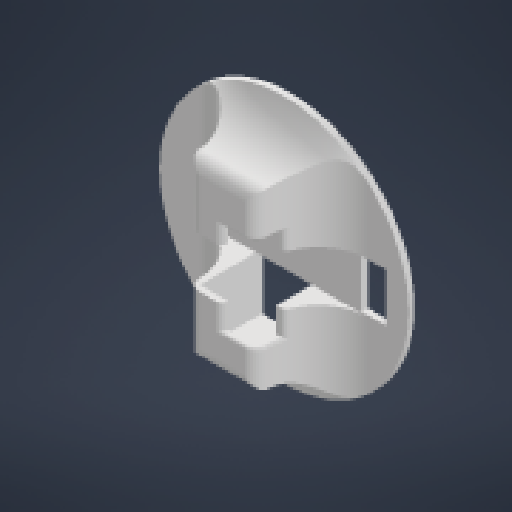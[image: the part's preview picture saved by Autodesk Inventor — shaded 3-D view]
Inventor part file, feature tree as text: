
AUTODESK INVENTOR PART (.ipt)
format: ipt  version: 2023 (Build 270158000, 158)  size: 404,480 bytes
history: native  units: mm
features: sketch x7, extrude x6, fillet x5
ambient origin geometry x8: Origin, YZ Plane, XZ Plane, XY Plane, X Axis, Y Axis, Z Axis, Center Point
bodies: Solid1 (feature_tree)
feature tree (18):
  extrude  "Extrusion1"  Depth=5.0mm TaperAngle=0.0deg
  extrude  "Extrusion2"  Depth=45.0mm
  extrude  "Extrusion3"  Depth=45.0mm
  fillet  "Fillet1"  Radius=40.0mm
  fillet  "Fillet2"  Radius=5.0mm
  extrude  "Extrusion4"  Depth=50.0mm TaperAngle=0.0deg
  extrude  "Extrusion5"  TaperAngle=90.0deg  [1 undecoded]
  fillet  "Fillet3"  Radius=22.5mm
  fillet  "Fillet4"  Radius=45.0mm
  fillet  "Fillet5"  Radius=45.0mm
  extrude  "Extrusion6"  Depth=50.0mm TaperAngle=0.0deg
  sketch  "Sketch7"  dims[d24=40.0mm d25=10.0mm d26=75.0mm d27=9.0mm d28=0.0mm d29=9.0mm d30=0.0mm d31=5.0mm d32=5.0mm d33=2.0mm d34=9.0mm d35=0.0mm d36=180.0deg]
  sketch  "Sketch1"  dims[d0=200.0mm d1=5.0mm d2=0.0mm]
  sketch  "Sketch2"  dims[d5=22.5mm d6=45.0mm]
  sketch  "Sketch3"  dims[d7=40.0mm d8=45.0mm d9=40.0mm d12=5.0mm]
  sketch  "Sketch4"  dims[d13=5.0mm d14=50.0mm d15=0.0mm]
  sketch  "Sketch5"  dims[d16=20.0mm d17=90.0deg d18=22.5mm d19=45.0mm d20=45.0mm]
  sketch  "Sketch6"  dims[d21=45.0mm d22=50.0mm d23=0.0mm]
note: 1 required parameter value undecoded (feature->parameter linkage not recoverable at this tier; creation-order binding heuristic only, values carry confidence <= 0.55)
